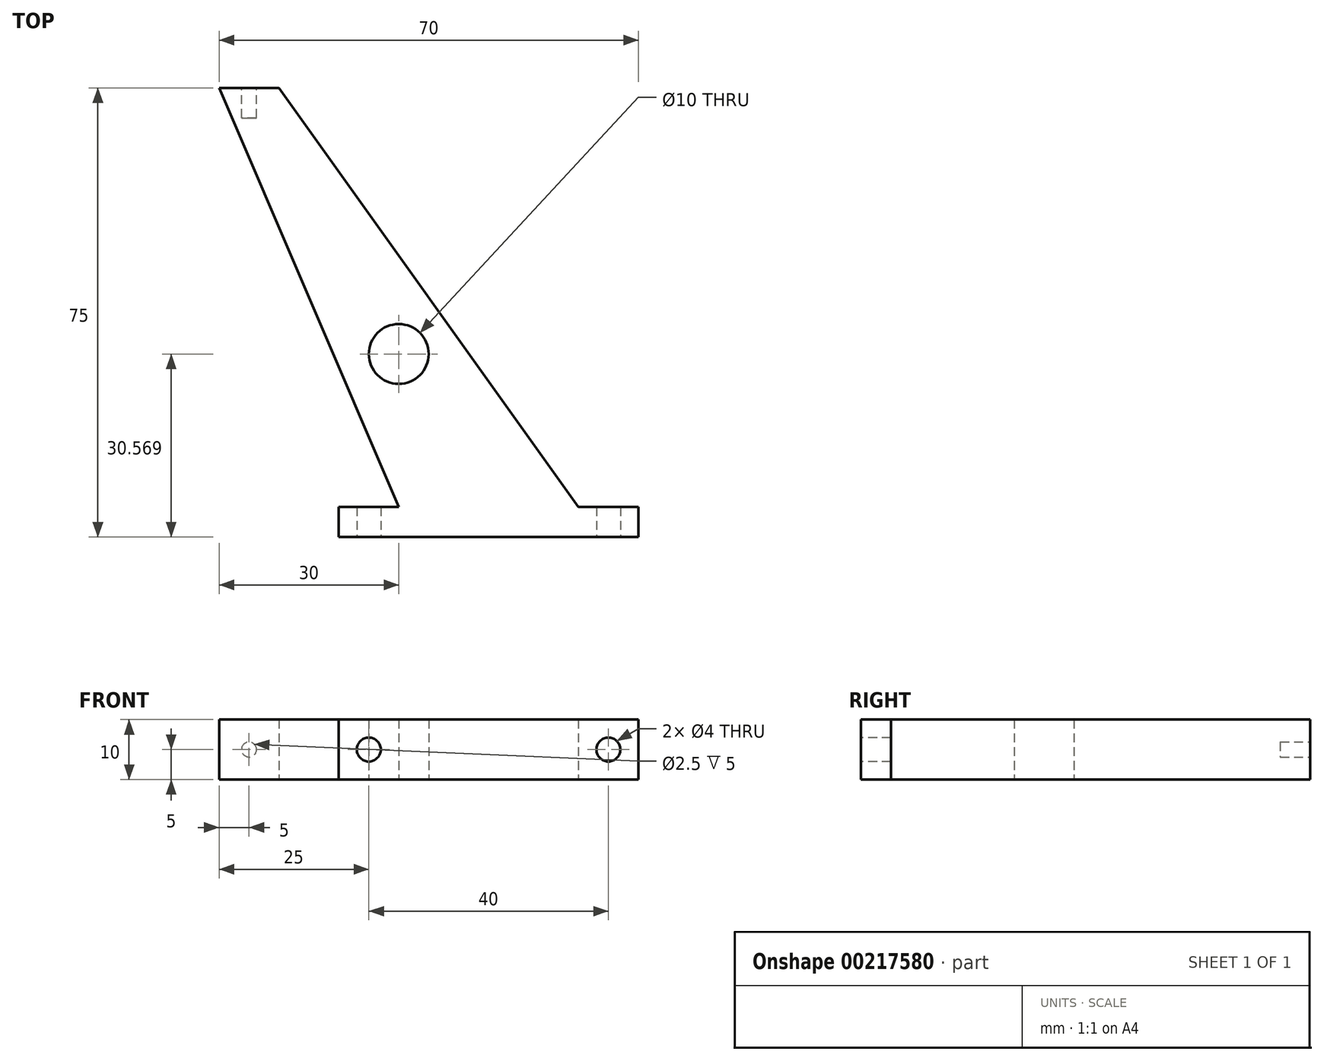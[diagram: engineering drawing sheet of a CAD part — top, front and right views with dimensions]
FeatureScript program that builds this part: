
annotation { "Feature Type Name" : "Feature", "Feature Type Description" : "" }
export const myFeature = defineFeature(function(context is Context, id is Id, definition is map)
    precondition{}
    {
        {
            var Q0;
            Q0=qCreatedBy(makeId("Top.planeOp"),FACE);
            var sketch = newSketch(context, id + "F0", { "sketchPlane" : qUnion([Q0])});
            skLineSegment(sketch, "E0.bottom", {"start": v(0, 0) * mm, "end": v(50, 0) * mm});
            skLineSegment(sketch, "E0.left", {"start": v(0, 0) * mm, "end": v(0, 5) * mm});
            skLineSegment(sketch, "E0.right", {"start": v(50, 0) * mm, "end": v(50, 5) * mm});
            skLineSegment(sketch, "E1", {"start": v(0, 5) * mm, "end": v(10, 5) * mm});
            skLineSegment(sketch, "E2", {"start": v(10, 5) * mm, "end": v(-20, 75) * mm});
            skLineSegment(sketch, "E3", {"start": v(50, 5) * mm, "end": v(40, 5) * mm});
            skLineSegment(sketch, "E4", {"start": v(10, 47) * mm, "end": v(10, 5) * mm, "construction": true});
            skLineSegment(sketch, "E5", {"start": v(-20, 75) * mm, "end": v(-10, 75) * mm});
            skLineSegment(sketch, "E6", {"start": v(-10, 75) * mm, "end": v(40, 5) * mm});
            skPoint(sketch, "E7.orphan", {"position": v(10, 75) * mm});
            skCircle(sketch, "E8", {"center": v(10, 30.57) * mm, "radius": 5 * mm});
            skSolve(sketch);
        }
        {
            var Q0;
            Q0=makeQuery(id+"F0.imprint","IMPRINT",FACE,{"disambiguationData":[TD([[makeQuery(id+"F0.imprint","IMPRINT",EDGE,{"derivedFrom":sQuery(id+"F0.wireOp",EDGE,"E0.bottom")}),1.0]])]});
            var Q1;
            Q1 = qConstructionFilter(qBodyType(qCreatedBy(id + "F0" ,EDGE), BodyType.WIRE), ConstructionObject.NO);
            extrude(context, id + "F1", {"entities" : qUnion([Q0]), "surfaceEntities" : qUnion([Q1]), "depth" : 10 * mm});
        }
        {
            var Q0;
            Q0=makeQuery(id+"F1.opExtrude","SWEPT_FACE",FACE,{"disambiguationData":[OSD([sQuery(id+"F0.wireOp",EDGE,"E0.bottom")])]});
            var sketch = newSketch(context, id + "F2", { "sketchPlane" : qUnion([Q0])});
            skLineSegment(sketch, "E9.bottom", {"start": v(50, 0) * mm, "end": v(45, 0) * mm, "construction": true});
            skLineSegment(sketch, "E9.top", {"start": v(50, 5) * mm, "end": v(45, 5) * mm, "construction": true});
            skLineSegment(sketch, "E9.left", {"start": v(50, 0) * mm, "end": v(50, 5) * mm, "construction": true});
            skLineSegment(sketch, "E9.right", {"start": v(45, 0) * mm, "end": v(45, 5) * mm, "construction": true});
            skLineSegment(sketch, "E10.bottom", {"start": v(0, 0) * mm, "end": v(5, 0) * mm, "construction": true});
            skLineSegment(sketch, "E10.top", {"start": v(0, 5) * mm, "end": v(5, 5) * mm, "construction": true});
            skLineSegment(sketch, "E10.left", {"start": v(0, 0) * mm, "end": v(0, 5) * mm, "construction": true});
            skLineSegment(sketch, "E10.right", {"start": v(5, 0) * mm, "end": v(5, 5) * mm, "construction": true});
            skCircle(sketch, "E11", {"center": v(45, 5) * mm, "radius": 2 * mm});
            skCircle(sketch, "E12", {"center": v(5, 5) * mm, "radius": 2 * mm});
            skSolve(sketch);
        }
        {
            var Q0;
            Q0=makeQuery(id+"F2.imprint","IMPRINT",FACE,{"disambiguationData":[TD([[makeQuery(id+"F2.imprint","IMPRINT",EDGE,{"derivedFrom":sQuery(id+"F2.wireOp",EDGE,"E11")}),1.0]])]});
            var Q1;
            Q1=makeQuery(id+"F2.imprint","IMPRINT",FACE,{"disambiguationData":[TD([[makeQuery(id+"F2.imprint","IMPRINT",EDGE,{"derivedFrom":sQuery(id+"F2.wireOp",EDGE,"E12")}),1.0]])]});
            extrude(context, id + "F3", {"entities" : qUnion([Q0, Q1]), "operationType" : NewBodyOperationType.REMOVE, "oppositeDirection" : true, "depth" : 5 * mm});
        }
        {
            var Q0;
            Q0=makeQuery(id+"F1.opExtrude","SWEPT_FACE",FACE,{"disambiguationData":[OSD([sQuery(id+"F0.wireOp",EDGE,"E5")])]});
            var sketch = newSketch(context, id + "F4", { "sketchPlane" : qUnion([Q0])});
            skLineSegment(sketch, "E13", {"start": v(20, 0) * mm, "end": v(10, 10) * mm, "construction": true});
            skCircle(sketch, "E14", {"center": v(15, 5) * mm, "radius": 1.25 * mm});
            skSolve(sketch);
        }
        {
            var Q0;
            Q0=makeQuery(id+"F4.imprint","IMPRINT",FACE,{"disambiguationData":[TD([[makeQuery(id+"F4.imprint","IMPRINT",EDGE,{"derivedFrom":sQuery(id+"F4.wireOp",EDGE,"E14")}),1.0]])]});
            extrude(context, id + "F5", {"entities" : qUnion([Q0]), "operationType" : NewBodyOperationType.REMOVE, "oppositeDirection" : true, "depth" : 5 * mm});
        }
    });
